# Revit family: Lyss 2.0
name_source: partatom
category: Lighting Fixtures
units: mm (PartAtom-declared; Revit-internal decimal feet)

## family parameters
Cut with Voids When Loaded = Yes
Host = Face
Light Source = Yes
Part Type = Normal
Room Calculation Point = Yes
Round Connector Dimension = Use Diameter
Shared = No

## types (1)
- Lyss 2.0 U 12°x160° (RGBW 19W 24Vdc)
    Apparent Load = 0 VA
    Apparent Load Phase 1 = 19 W
    Body = L&L_Die Cast aluminium
    CRI = -
    Code = -
    Color Filter = 16777215
    Control system = -
    Cutout dimensions = -
    Default Elevation = 1219 mm
    Delivered lumen output = 256 lm, R: 31 lm G: 85 lm B: 30 lm W: 110 lm (4000K)
    Description = Projector for outdoor applications
    Dimming Lamp Color Temperature Shift = <None>
    Emit from Line Length = 610 mm
    Energy efficiency class = A A+ A++
    Features = -
    Height mm = 66 mm  [stored 0.216535 ft]
    IP = IP65
    LED Colour = RGBW
    Length mm = 118 mm
    Lens = L&L_Polycarbonate
    Lumen output at source = 1024 lm, R: 124 lm G: 340 lm B: 120 lm W: 440 lm (4000K)
    Manufacturer = L&L Luce&Light
    Material = body in die-cast aluminium, screen in polycarbonate
    Model = Lyss 2.0
    Mounting = surface mounted (windowsill, arch)
    No. and type of led = 4 RGBW LEDs groups, 50 000h L90 B10 (Ta 25°C)
    Notes = -
    Optics = 12°x160°
    Photometric Web File = LYSS 2.0 U 12°x160° [RGBW 19W 24Vdc].IES
    Power = 19W
    Power cables = includes 1.5 m FEP+RUB cable (equivalent to H05RN-F) 6x0.50/0.50 Ø6.3 mm
    Power supply = 24Vdc
    Power supply unit = not included
    Screen = L&L_Polycarbonate(1)
    Tilt Angle = 90.00°
    Tiltable = -
    URL = https://www.lucelight.it
    URL Accessories and power supply units = https://www.lucelight.it
    URL Catalogue = https://www.lucelight.it
    URL DXF = https://www.lucelight.it
    URL Description = https://www.lucelight.it
    URL General code = https://www.lucelight.it
    URL IES Photometric file = https://www.lucelight.it
    URL Image = https://www.lucelight.it
    URL Technical sheet = https://www.lucelight.it
    Voltage = 24 V
    Weight kg = 0.70 kg
    Width mm = 88 mm  [stored 0.288714 ft]
    Wiring = parallel

note: [stored X ft] marks values corroborated as IEEE doubles in the binary element streams (Revit-internal decimal feet)

## geometry (parser evidence)
native form markers: Blend x2, Sweep x6
no freeform markers — native parametric forms only
